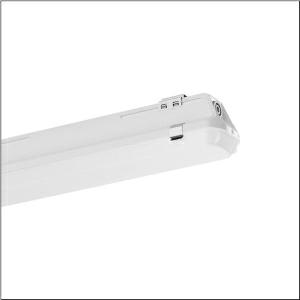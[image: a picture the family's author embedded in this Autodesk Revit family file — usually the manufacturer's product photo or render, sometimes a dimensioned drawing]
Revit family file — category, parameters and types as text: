
# Revit family: monsun_r__11_51fp207p460h_8ebd
name_source: partatom
category: Lighting Fixtures
units: mm (PartAtom-declared; Revit-internal decimal feet)

## family parameters
Cut with Voids When Loaded = No
Host = Face
Light Source = No
Part Type = Normal
Room Calculation Point = No
Round Connector Dimension = Use Diameter
Shared = No

## types (1)
- Monsun® 11 (1 x LED, 6030 lm, 37.7 W, 4000K)
    Apparent Load = 38 VA
    CIE Flux Codes = 45 75 93 94 100
    Color Rendering = 80
    Color Temperature = 4000K
    Default Elevation = 1800 mm
    Description = Monsun® 11, damp-proof luminaire, chain hanger, primary optical cover: enclosure, of PC, light emission: direct distribution, primary light characteristic: symmetric, installation type: suspended mounting, surface-mounted, horizontal mounting, vertical mounting, LED, rated luminous flux: 6.030lm, luminous efficacy: 160lm/W, light colour: 840, colour temperature: 4000K, control gear: ECG, with terminal, 3-pole, max. 2.5mm², mains connection: 220..240V, AC, 50/60Hz, rated input power: 38W, luminaire housing, of glass-fibre reinforced polyester, uncoated, bright grey, incl. chain hanger, length: 1.590mm, width: 90mm, height: 88mm, clip for enclosure, of stainless steel (V2A), ceiling mounting element, of stainless steel (V2A), chain hanger, of stainless steel (V2A), protection rating (complete): IP66, insulation class (complete): insulation class I (protective earthing), certification: CE, ENEC, VDE, UKCA, protection symbol: D, impact resistance: IK08, permissible operating ambient temperature: -35..+40°C, standard: EN 50419, EN 60598-2-1, no direct snow, no direct sun, no direct rain, for indoor or canopied outdoor use, corresponds to IFS (International Featured Standards) requirements for safety and quality in the food industry, contact your sales advisor before using the luminaires in applications with unclear chemical exposure, large temperature fluctuations or condensation-forming humidity, LABS conformity tested according to VDMA 24364:2018-05, packaging unit: 1 piece
    Height = 89 mm
    Lamp = 1 x LED
    Lamp Light Flux = 6030 lm
    Lamp Power = 37.7 W
    Lamp count = 1
    Length = 1590 mm
    Luminous efficacy = 160 lm/W
    Manufacturer = Siteco
    ModVariant = No
    Model = 51FP207P460H
    Mounting Place = Ceiling
    Mounting Type = Surface mounted
    Number of Poles = 1
    OnlyDefault = Yes
    Power Factor = 1
    Product Name = Monsun® 11
    Product group = damp-proof luminaire
    ProductGroupID = 300
    Protection Class = Protection class I
    Protection Degree = IP 66
    RLX_Detail_Level = 1
    RLX_Emergency_Light_Flux = 0 lm
    RLX_Emergency_Type = 0
    RLX_Emergency_Type_DB = No
    RlxData = <blob elided: 88705 chars, md5=c584174e>
    Socket = socket
    Standby Power = 0 W
    System Light Flux = 6030 lm
    System Power = 38 W
    Type Comments = Product without accessories
    Type Image = l_1004748.jpg
    URL = http://relux.com
    VarID = ---
    Voltage = 0 V
    Weight = 0.00 kg
    Width = 90 mm

## geometry (parser evidence)
native form markers: Blend x4, Sweep x13
no freeform markers — native parametric forms only
